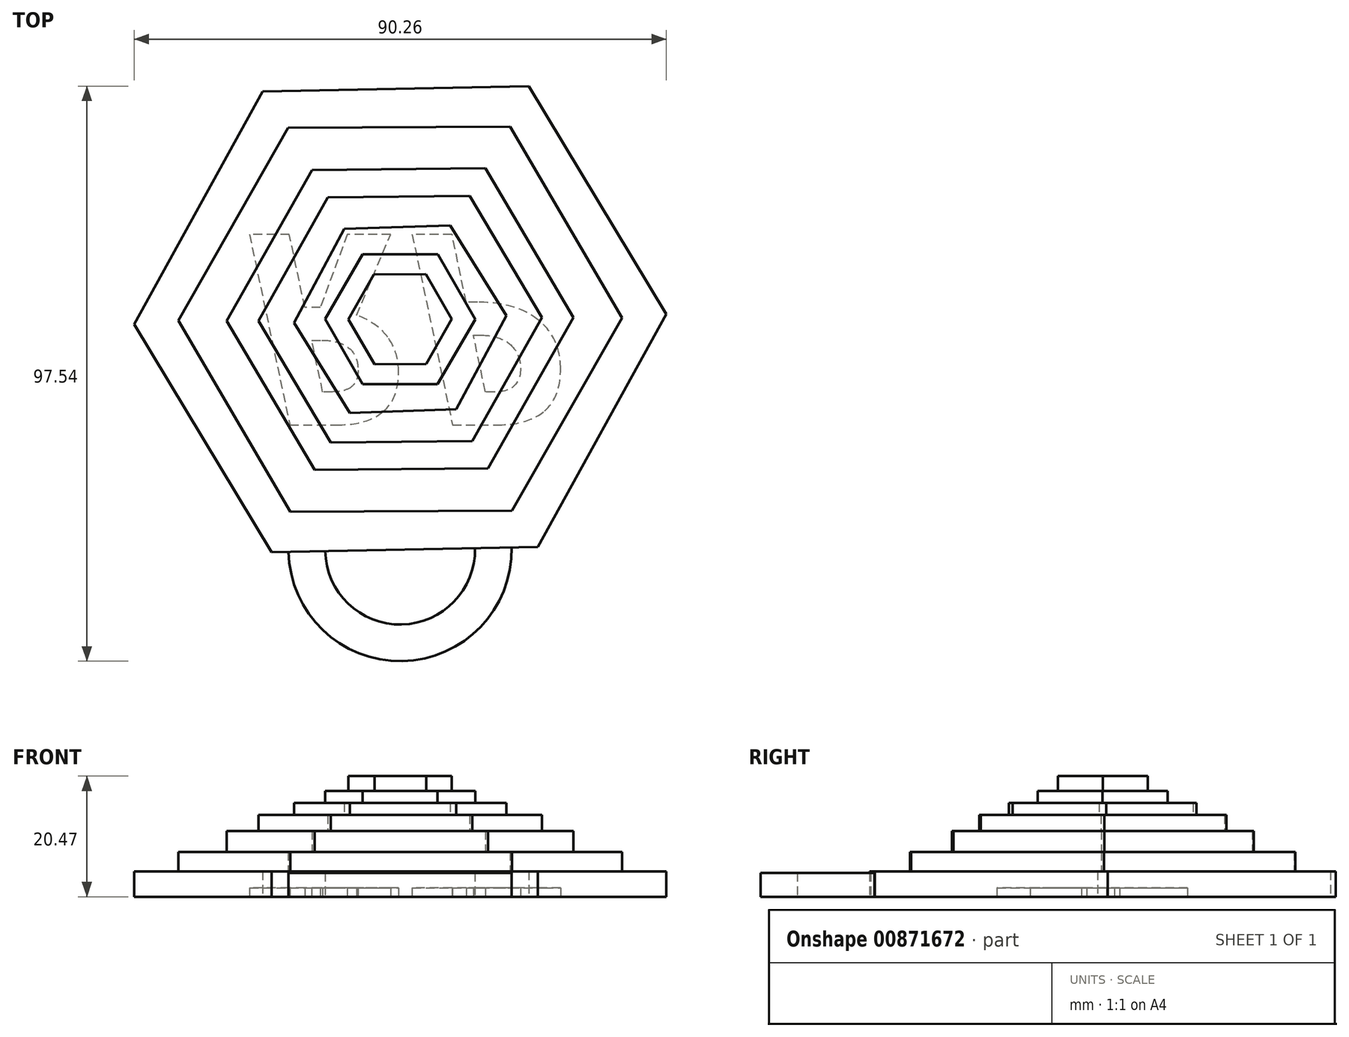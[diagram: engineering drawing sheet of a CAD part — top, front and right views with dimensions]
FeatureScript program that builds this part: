
annotation { "Feature Type Name" : "Feature", "Feature Type Description" : "" }
export const myFeature = defineFeature(function(context is Context, id is Id, definition is map)
    precondition{}
    {
        {
            var Q0;
            Q0=qCreatedBy(makeId("Top.planeOp"),FACE);
            var sketch = newSketch(context, id + "F0", { "sketchPlane" : qUnion([Q0])});
            skCircle(sketch, "E0.cCircle", {"center": v(0, 0) * mm, "radius": 39.09 * mm, "construction": true});
            skLineSegment(sketch, "E0.0", {"start": v(45.13, 0.88) * mm, "end": v(23.32, -38.64) * mm});
            skLineSegment(sketch, "E0.1", {"start": v(23.32, -38.64) * mm, "end": v(-21.8, -39.52) * mm});
            skLineSegment(sketch, "E0.2", {"start": v(-21.8, -39.52) * mm, "end": v(-45.13, -0.88) * mm});
            skLineSegment(sketch, "E0.3", {"start": v(-45.13, -0.88) * mm, "end": v(-23.32, 38.64) * mm});
            skLineSegment(sketch, "E0.4", {"start": v(-23.32, 38.64) * mm, "end": v(21.8, 39.52) * mm});
            skLineSegment(sketch, "E0.5", {"start": v(21.8, 39.52) * mm, "end": v(45.13, 0.88) * mm});
            skPoint(sketch, "E0.0.midPoint", {"position": v(34.22, -18.88) * mm});
            skSolve(sketch);
        }
        {
            var Q0;
            Q0=makeQuery(id+"F0.imprint","IMPRINT",FACE,{"disambiguationData":[TD([[makeQuery(id+"F0.imprint","IMPRINT",EDGE,{"derivedFrom":sQuery(id+"F0.wireOp",EDGE,"E0.0")}),-1.0]])]});
            extrude(context, id + "F1", {"entities" : qUnion([Q0]), "depth" : 4.32 * mm, "offsetDistance" : 25.4 * mm});
        }
        {
            var Q0;
            Q0=makeQuery(id+"F1.opExtrude","CAP_FACE",FACE,{"disambiguationData":[OSD([sQuery(id+"F0.wireOp",EDGE,"E0.0"),sQuery(id+"F0.wireOp",EDGE,"E0.1"),sQuery(id+"F0.wireOp",EDGE,"E0.2"),sQuery(id+"F0.wireOp",EDGE,"E0.3"),sQuery(id+"F0.wireOp",EDGE,"E0.4"),sQuery(id+"F0.wireOp",EDGE,"E0.5")])],"isStart":false});
            var sketch = newSketch(context, id + "F2", { "sketchPlane" : qUnion([Q0])});
            skCircle(sketch, "E1.cCircle", {"center": v(0, 0) * mm, "radius": 32.58 * mm, "construction": true});
            skLineSegment(sketch, "E1.0", {"start": v(37.61, 0.2) * mm, "end": v(18.99, -32.47) * mm});
            skLineSegment(sketch, "E1.1", {"start": v(18.99, -32.47) * mm, "end": v(-18.63, -32.68) * mm});
            skLineSegment(sketch, "E1.2", {"start": v(-18.63, -32.68) * mm, "end": v(-37.61, -0.2) * mm});
            skLineSegment(sketch, "E1.3", {"start": v(-37.61, -0.2) * mm, "end": v(-18.99, 32.47) * mm});
            skLineSegment(sketch, "E1.4", {"start": v(-18.99, 32.47) * mm, "end": v(18.63, 32.68) * mm});
            skLineSegment(sketch, "E1.5", {"start": v(18.63, 32.68) * mm, "end": v(37.61, 0.2) * mm});
            skPoint(sketch, "E1.0.midPoint", {"position": v(28.3, -16.13) * mm});
            skSolve(sketch);
        }
        {
            var Q0;
            Q0=makeQuery(id+"F2.imprint","IMPRINT",FACE,{"disambiguationData":[TD([[makeQuery(id+"F2.imprint","IMPRINT",EDGE,{"derivedFrom":sQuery(id+"F2.wireOp",EDGE,"E1.0")}),-1.0]])]});
            extrude(context, id + "F3", {"entities" : qUnion([Q0]), "operationType" : NewBodyOperationType.ADD, "depth" : 3.3 * mm, "offsetDistance" : 25.4 * mm});
        }
        {
            var Q0;
            Q0=makeQuery(id+"F3.opExtrude","CAP_FACE",FACE,{"disambiguationData":[OSD([sQuery(id+"F2.wireOp",EDGE,"E1.0"),sQuery(id+"F2.wireOp",EDGE,"E1.1"),sQuery(id+"F2.wireOp",EDGE,"E1.2"),sQuery(id+"F2.wireOp",EDGE,"E1.3"),sQuery(id+"F2.wireOp",EDGE,"E1.4"),sQuery(id+"F2.wireOp",EDGE,"E1.5")])],"isStart":false});
            var sketch = newSketch(context, id + "F4", { "sketchPlane" : qUnion([Q0])});
            skCircle(sketch, "E2.cCircle", {"center": v(0, 0) * mm, "radius": 25.46 * mm, "construction": true});
            skLineSegment(sketch, "E2.0", {"start": v(29.4, 0.26) * mm, "end": v(14.93, -25.33) * mm});
            skLineSegment(sketch, "E2.1", {"start": v(14.93, -25.33) * mm, "end": v(-14.48, -25.6) * mm});
            skLineSegment(sketch, "E2.2", {"start": v(-14.48, -25.6) * mm, "end": v(-29.4, -0.26) * mm});
            skLineSegment(sketch, "E2.3", {"start": v(-29.4, -0.26) * mm, "end": v(-14.93, 25.33) * mm});
            skLineSegment(sketch, "E2.4", {"start": v(-14.93, 25.33) * mm, "end": v(14.48, 25.6) * mm});
            skLineSegment(sketch, "E2.5", {"start": v(14.48, 25.6) * mm, "end": v(29.4, 0.26) * mm});
            skPoint(sketch, "E2.0.midPoint", {"position": v(22.16, -12.54) * mm});
            skSolve(sketch);
        }
        {
            var Q0;
            Q0=makeQuery(id+"F4.imprint","IMPRINT",FACE,{"disambiguationData":[TD([[makeQuery(id+"F4.imprint","IMPRINT",EDGE,{"derivedFrom":sQuery(id+"F4.wireOp",EDGE,"E2.0")}),-1.0]])]});
            extrude(context, id + "F5", {"entities" : qUnion([Q0]), "operationType" : NewBodyOperationType.ADD, "depth" : 3.56 * mm, "offsetDistance" : 25.4 * mm});
        }
        {
            var Q0;
            Q0=makeQuery(id+"F5.opExtrude","CAP_FACE",FACE,{"disambiguationData":[OSD([sQuery(id+"F4.wireOp",EDGE,"E2.0"),sQuery(id+"F4.wireOp",EDGE,"E2.1"),sQuery(id+"F4.wireOp",EDGE,"E2.2"),sQuery(id+"F4.wireOp",EDGE,"E2.3"),sQuery(id+"F4.wireOp",EDGE,"E2.4"),sQuery(id+"F4.wireOp",EDGE,"E2.5")])],"isStart":false});
            var sketch = newSketch(context, id + "F6", { "sketchPlane" : qUnion([Q0])});
            skCircle(sketch, "E3.cCircle", {"center": v(0, 0) * mm, "radius": 20.82 * mm, "construction": true});
            skLineSegment(sketch, "E3.0", {"start": v(24.04, 0.27) * mm, "end": v(12.25, -20.68) * mm});
            skLineSegment(sketch, "E3.1", {"start": v(12.25, -20.68) * mm, "end": v(-11.79, -20.95) * mm});
            skLineSegment(sketch, "E3.2", {"start": v(-11.79, -20.95) * mm, "end": v(-24.04, -0.27) * mm});
            skLineSegment(sketch, "E3.3", {"start": v(-24.04, -0.27) * mm, "end": v(-12.25, 20.68) * mm});
            skLineSegment(sketch, "E3.4", {"start": v(-12.25, 20.68) * mm, "end": v(11.79, 20.95) * mm});
            skLineSegment(sketch, "E3.5", {"start": v(11.79, 20.95) * mm, "end": v(24.04, 0.27) * mm});
            skPoint(sketch, "E3.0.midPoint", {"position": v(18.14, -10.2) * mm});
            skSolve(sketch);
        }
        {
            var Q0;
            Q0=makeQuery(id+"F6.imprint","IMPRINT",FACE,{"disambiguationData":[TD([[makeQuery(id+"F6.imprint","IMPRINT",EDGE,{"derivedFrom":sQuery(id+"F6.wireOp",EDGE,"E3.0")}),-1.0]])]});
            extrude(context, id + "F7", {"entities" : qUnion([Q0]), "operationType" : NewBodyOperationType.ADD, "depth" : 2.7 * mm, "offsetDistance" : 25.4 * mm});
        }
        {
            var Q0;
            Q0=makeQuery(id+"F7.opExtrude","CAP_FACE",FACE,{"disambiguationData":[OSD([sQuery(id+"F6.wireOp",EDGE,"E3.0"),sQuery(id+"F6.wireOp",EDGE,"E3.1"),sQuery(id+"F6.wireOp",EDGE,"E3.2"),sQuery(id+"F6.wireOp",EDGE,"E3.3"),sQuery(id+"F6.wireOp",EDGE,"E3.4"),sQuery(id+"F6.wireOp",EDGE,"E3.5")])],"isStart":false});
            var sketch = newSketch(context, id + "F8", { "sketchPlane" : qUnion([Q0])});
            skCircle(sketch, "E4.cCircle", {"center": v(0, 0) * mm, "radius": 15.6 * mm, "construction": true});
            skLineSegment(sketch, "E4.0", {"start": v(18, 0.58) * mm, "end": v(9.5, -15.3) * mm});
            skLineSegment(sketch, "E4.1", {"start": v(9.5, -15.3) * mm, "end": v(-8.5, -15.88) * mm});
            skLineSegment(sketch, "E4.2", {"start": v(-8.5, -15.88) * mm, "end": v(-18, -0.58) * mm});
            skLineSegment(sketch, "E4.3", {"start": v(-18, -0.58) * mm, "end": v(-9.5, 15.3) * mm});
            skLineSegment(sketch, "E4.4", {"start": v(-9.5, 15.3) * mm, "end": v(8.5, 15.88) * mm});
            skLineSegment(sketch, "E4.5", {"start": v(8.5, 15.88) * mm, "end": v(18, 0.58) * mm});
            skPoint(sketch, "E4.0.midPoint", {"position": v(13.76, -7.36) * mm});
            skSolve(sketch);
        }
        {
            var Q0;
            Q0=makeQuery(id+"F8.imprint","IMPRINT",FACE,{"disambiguationData":[TD([[makeQuery(id+"F8.imprint","IMPRINT",EDGE,{"derivedFrom":sQuery(id+"F8.wireOp",EDGE,"E4.0")}),-1.0]])]});
            extrude(context, id + "F9", {"entities" : qUnion([Q0]), "operationType" : NewBodyOperationType.ADD, "depth" : 2.03 * mm, "offsetDistance" : 25.4 * mm});
        }
        {
            var Q0;
            Q0=makeQuery(id+"F9.opExtrude","CAP_FACE",FACE,{"disambiguationData":[OSD([sQuery(id+"F8.wireOp",EDGE,"E4.0"),sQuery(id+"F8.wireOp",EDGE,"E4.1"),sQuery(id+"F8.wireOp",EDGE,"E4.2"),sQuery(id+"F8.wireOp",EDGE,"E4.3"),sQuery(id+"F8.wireOp",EDGE,"E4.4"),sQuery(id+"F8.wireOp",EDGE,"E4.5")])],"isStart":false});
            var sketch = newSketch(context, id + "F10", { "sketchPlane" : qUnion([Q0])});
            skCircle(sketch, "E5.cCircle", {"center": v(0, 0) * mm, "radius": 11.03 * mm, "construction": true});
            skLineSegment(sketch, "E5.0", {"start": v(12.74, -0.01) * mm, "end": v(6.36, -11.04) * mm});
            skLineSegment(sketch, "E5.1", {"start": v(6.36, -11.04) * mm, "end": v(-6.38, -11.02) * mm});
            skLineSegment(sketch, "E5.2", {"start": v(-6.38, -11.02) * mm, "end": v(-12.74, 0.01) * mm});
            skLineSegment(sketch, "E5.3", {"start": v(-12.74, 0.01) * mm, "end": v(-6.36, 11.04) * mm});
            skLineSegment(sketch, "E5.4", {"start": v(-6.36, 11.04) * mm, "end": v(6.38, 11.02) * mm});
            skLineSegment(sketch, "E5.5", {"start": v(6.38, 11.02) * mm, "end": v(12.74, -0.01) * mm});
            skPoint(sketch, "E5.0.midPoint", {"position": v(9.55, -5.52) * mm});
            skSolve(sketch);
        }
        {
            var Q0;
            Q0=makeQuery(id+"F10.imprint","IMPRINT",FACE,{"disambiguationData":[TD([[makeQuery(id+"F10.imprint","IMPRINT",EDGE,{"derivedFrom":sQuery(id+"F10.wireOp",EDGE,"E5.0")}),-1.0]])]});
            extrude(context, id + "F11", {"entities" : qUnion([Q0]), "operationType" : NewBodyOperationType.ADD, "depth" : 2.03 * mm, "offsetDistance" : 25.4 * mm});
        }
        {
            var Q0;
            Q0=makeQuery(id+"F11.opExtrude","CAP_FACE",FACE,{"disambiguationData":[OSD([sQuery(id+"F10.wireOp",EDGE,"E5.0"),sQuery(id+"F10.wireOp",EDGE,"E5.1"),sQuery(id+"F10.wireOp",EDGE,"E5.2"),sQuery(id+"F10.wireOp",EDGE,"E5.3"),sQuery(id+"F10.wireOp",EDGE,"E5.4"),sQuery(id+"F10.wireOp",EDGE,"E5.5")])],"isStart":false});
            var sketch = newSketch(context, id + "F12", { "sketchPlane" : qUnion([Q0])});
            skCircle(sketch, "E6.cCircle", {"center": v(0, 0) * mm, "radius": 7.6 * mm, "construction": true});
            skLineSegment(sketch, "E6.0", {"start": v(8.78, 0.04) * mm, "end": v(4.43, -7.58) * mm});
            skLineSegment(sketch, "E6.1", {"start": v(4.43, -7.58) * mm, "end": v(-4.35, -7.62) * mm});
            skLineSegment(sketch, "E6.2", {"start": v(-4.35, -7.62) * mm, "end": v(-8.78, -0.04) * mm});
            skLineSegment(sketch, "E6.3", {"start": v(-8.78, -0.04) * mm, "end": v(-4.43, 7.58) * mm});
            skLineSegment(sketch, "E6.4", {"start": v(-4.43, 7.58) * mm, "end": v(4.35, 7.62) * mm});
            skLineSegment(sketch, "E6.5", {"start": v(4.35, 7.62) * mm, "end": v(8.78, 0.04) * mm});
            skPoint(sketch, "E6.0.midPoint", {"position": v(6.6, -3.77) * mm});
            skSolve(sketch);
        }
        {
            var Q0;
            Q0=makeQuery(id+"F12.imprint","IMPRINT",FACE,{"disambiguationData":[TD([[makeQuery(id+"F12.imprint","IMPRINT",EDGE,{"derivedFrom":sQuery(id+"F12.wireOp",EDGE,"E6.0")}),-1.0]])]});
            extrude(context, id + "F13", {"entities" : qUnion([Q0]), "operationType" : NewBodyOperationType.ADD, "depth" : 2.54 * mm, "offsetDistance" : 25.4 * mm});
        }
        {
            var Q0;
            Q0=makeQuery(id+"F1.opExtrude","CAP_FACE",FACE,{"disambiguationData":[OSD([sQuery(id+"F0.wireOp",EDGE,"E0.0"),sQuery(id+"F0.wireOp",EDGE,"E0.1"),sQuery(id+"F0.wireOp",EDGE,"E0.2"),sQuery(id+"F0.wireOp",EDGE,"E0.3"),sQuery(id+"F0.wireOp",EDGE,"E0.4"),sQuery(id+"F0.wireOp",EDGE,"E0.5")])],"isStart":true});
            var sketch = newSketch(context, id + "F14", { "sketchPlane" : qUnion([Q0])});
            skText(sketch, "E7", { "text": "RP", "fontName": "OpenSans-BoldItalic.ttf"});
            const initialGuessF14  = {"E7": [-0.02672, -0.01441, 1, 0, 0.03263]};
            skSetInitialGuess(sketch, initialGuessF14);
            skSolve(sketch);
        }
        {
            var Q0;
            Q0 = qSketchRegion(id + "F14", true);
            extrude(context, id + "F15", {"entities" : qUnion([Q0]), "operationType" : NewBodyOperationType.REMOVE, "oppositeDirection" : true, "depth" : 1.52 * mm, "offsetDistance" : 25.4 * mm});
        }
        {
            var Q0;
            {var subQ0=sQuery(id+"F0.wireOp",EDGE,"E0.0");var subQ1=sQuery(id+"F0.wireOp",EDGE,"E0.2");var subQ2=sQuery(id+"F0.wireOp",EDGE,"E0.1");var subQ3=sQuery(id+"F0.wireOp",EDGE,"E0.3");var subQ4=sQuery(id+"F0.wireOp",EDGE,"E0.4");var subQ5=sQuery(id+"F0.wireOp",EDGE,"E0.5");Q0=makeQuery(id+"F15.boolean.opBoolean","SPLIT",FACE,{"disambiguationData":[TD([makeQuery(id+"F1.opExtrude","SWEPT_FACE",FACE,{"disambiguationData":[OSD([subQ0])]})])],"derivedFrom":makeQuery(id+"F1.opExtrude","CAP_FACE",FACE,{"disambiguationData":[OSD([subQ0,subQ2,subQ1,subQ3,subQ4,subQ5])],"isStart":true})});}
            var sketch = newSketch(context, id + "F16", { "sketchPlane" : qUnion([Q0])});
            skCircle(sketch, "E8", {"center": v(0, 39.1) * mm, "radius": 18.92 * mm});
            skCircle(sketch, "E9", {"center": v(0, 39.1) * mm, "radius": 12.7 * mm});
            skSolve(sketch);
        }
        {
            var Q0;
            {var subQ0=sQuery(id+"F16.wireOp",EDGE,"E8");var subQ1=makeQuery(id+"F1.opExtrude","CAP_EDGE",EDGE,{"disambiguationData":[OSD([sQuery(id+"F0.wireOp",EDGE,"E0.1")])],"isStart":true});var subQ2=makeQuery(id+"F16.imprint","INTERSECT",VERTEX,{"disambiguationData":[OD(0.0)],"derivedFrom":[subQ1,subQ0]});Q0=makeQuery(id+"F16.imprint","IMPRINT",FACE,{"disambiguationData":[TD([[makeQuery(id+"F16.imprint","IMPRINT",EDGE,{"disambiguationData":[TD([[subQ2,-1.0]])],"derivedFrom":subQ0}),1.0]])]});}
            extrude(context, id + "F17", {"entities" : qUnion([Q0]), "operationType" : NewBodyOperationType.ADD, "oppositeDirection" : true, "depth" : 4.06 * mm, "offsetDistance" : 25.4 * mm});
        }
    });
